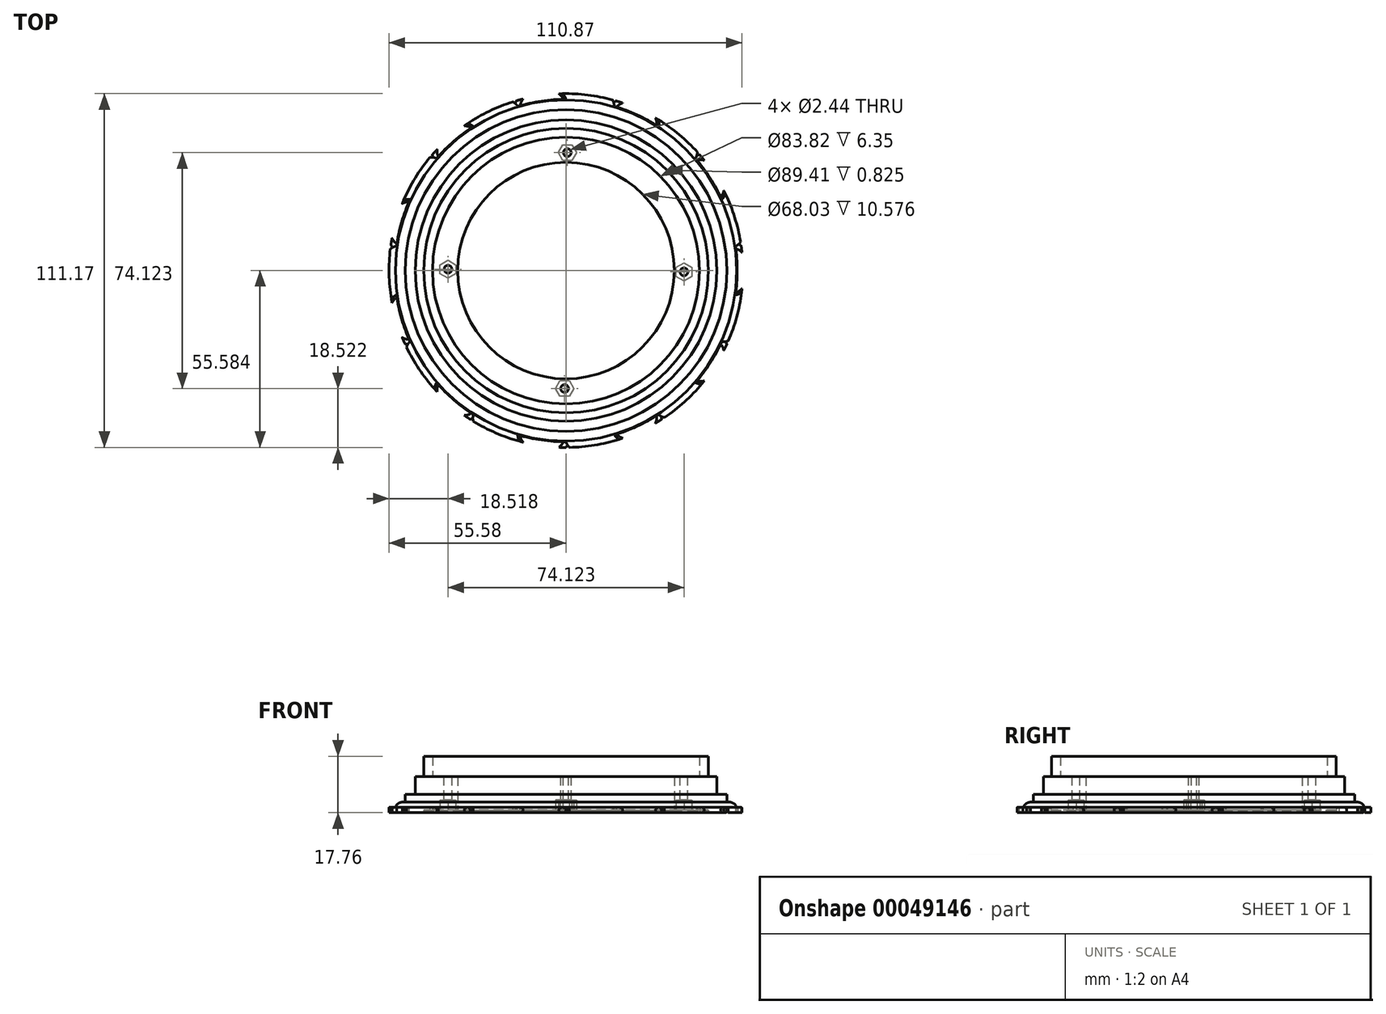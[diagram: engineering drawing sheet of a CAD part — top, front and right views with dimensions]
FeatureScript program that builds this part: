
annotation { "Feature Type Name" : "Feature", "Feature Type Description" : "" }
export const myFeature = defineFeature(function(context is Context, id is Id, definition is map)
    precondition{}
    {
        {
            assignVariable(context, id + "F0", {"name" : "numTeeth", "anyValue" : 11});
        }
        {
            var Q0;
            Q0=qCreatedBy(makeId("Top.planeOp"),FACE);
            var sketch = newSketch(context, id + "F1", { "sketchPlane" : qUnion([Q0])});
            skCircle(sketch, "E0", {"center": v(0, 0) * mm, "radius": 57.15 * mm, "construction": true});
            skLineSegment(sketch, "E1", {"start": v(0, 0) * mm, "end": v(0, 57.15) * mm, "construction": true});
            skCircle(sketch, "E2", {"center": v(0, 3.34) * mm, "radius": 53.8 * mm});
            skCircle(sketch, "E3", {"center": v(0, 3.34) * mm, "radius": 3.34 * mm, "construction": true});
            skLineSegment(sketch, "E4", {"start": v(0, 3.34) * mm, "end": v(-29.09, 48.6) * mm, "construction": true});
            skLineSegment(sketch, "E5", {"start": v(0, 57.15) * mm, "end": v(-29.09, 48.6) * mm, "construction": true});
            skLineSegment(sketch, "E6", {"start": v(-14.54, 52.88) * mm, "end": v(-29.09, 48.6) * mm, "construction": true});
            skLineSegment(sketch, "E7", {"start": v(-14.02, 24.18) * mm, "end": v(-21.82, 50.74) * mm, "construction": true});
            skCircle(sketch, "E8", {"center": v(-14.54, 52.88) * mm, "radius": 7.58 * mm, "construction": true});
            skLineSegment(sketch, "E9", {"start": v(-15.16, 54.97) * mm, "end": v(-16.68, 60.15) * mm, "construction": true});
            skEllipticalArc(sketch, "E10", {});
            skPoint(sketch, "E11", {"position": v(-15.16, 54.97) * mm});
            skLineSegment(sketch, "E12", {"start": v(-15.16, 54.97) * mm, "end": v(0, 54.97) * mm, "construction": true});
            skPoint(sketch, "E13", {"position": v(-7.58, 54.97) * mm});
            skCircle(sketch, "E14", {"center": v(0, 54.97) * mm, "radius": 7.58 * mm, "construction": true});
            skPoint(sketch, "E15", {"position": v(0, 62.55) * mm});
            skEllipticalArc(sketch, "E16", {});
            skCircle(sketch, "E17", {"center": v(0, 3.34) * mm, "radius": 44.7 * mm});
            skEllipticalArc(sketch, "E18.trimOffspring", {});
            skEllipticalArc(sketch, "E19.trimOffspring", {});
            skLineSegment(sketch, "E20", {"start": v(0, 3.34) * mm, "end": v(-8.33, 61.3) * mm, "construction": true});
            skCircle(sketch, "E21", {"center": v(0, 3.34) * mm, "radius": 55.58 * mm});
            skCircle(sketch, "E22", {"center": v(0, 3.34) * mm, "radius": 127 * mm});
            skLineSegment(sketch, "E23", {"start": v(0, 3.34) * mm, "end": v(-127, 3.34) * mm, "construction": true});
            skLineSegment(sketch, "E24", {"start": v(-53.8, 3.34) * mm, "end": v(-55.58, 3.34) * mm, "construction": true});
            skFitSpline(sketch, "E25.0", {"points": [v(-14.94, 56.45) * mm, v(-15.23, 54.97) * mm, v(-14.94, 53.49) * mm, v(-14.22, 52.3) * mm, v(-13.37, 51.41) * mm, v(-12.35, 50.56) * mm, v(-10.78, 49.6) * mm, v(-8.86, 48.81) * mm, v(-7.15, 48.3) * mm, v(-5.35, 47.87) * mm, v(-3.45, 47.59) * mm, v(-1.5, 47.44) * mm, v(0, 47.4) * mm, v(1.5, 47.44) * mm, v(3.45, 47.59) * mm, v(5.35, 47.87) * mm, v(7.15, 48.3) * mm, v(8.86, 48.81) * mm, v(10.78, 49.6) * mm, v(12.35, 50.56) * mm, v(13.37, 51.41) * mm, v(14.22, 52.3) * mm, v(14.94, 53.49) * mm, v(15.23, 54.97) * mm, v(14.94, 56.45) * mm, v(14.22, 57.63) * mm, v(13.37, 58.53) * mm, v(12.35, 59.38) * mm, v(10.78, 60.34) * mm, v(8.86, 61.13) * mm, v(7.15, 61.64) * mm, v(5.35, 62.07) * mm, v(3.45, 62.35) * mm, v(1.5, 62.5) * mm, v(0, 62.54) * mm, v(-1.5, 62.5) * mm, v(-3.45, 62.35) * mm, v(-5.35, 62.07) * mm, v(-7.15, 61.64) * mm, v(-8.86, 61.13) * mm, v(-10.78, 60.34) * mm, v(-12.35, 59.38) * mm, v(-13.37, 58.53) * mm, v(-14.22, 57.63) * mm, v(-14.94, 56.45) * mm, v(-15.23, 54.97) * mm, v(-14.94, 53.49) * mm]});
            skFitSpline(sketch, "E25.1", {"points": [v(0.2, 55.67) * mm, v(0.07, 57.17) * mm, v(-0.63, 58.5) * mm, v(-1.65, 59.44) * mm, v(-2.71, 60.06) * mm, v(-3.94, 60.6) * mm, v(-5.72, 61.07) * mm, v(-7.78, 61.28) * mm, v(-9.57, 61.3) * mm, v(-11.4, 61.2) * mm, v(-13.31, 60.94) * mm, v(-15.23, 60.52) * mm, v(-16.68, 60.14) * mm, v(-18.1, 59.68) * mm, v(-19.94, 59) * mm, v(-21.68, 58.18) * mm, v(-23.28, 57.27) * mm, v(-24.78, 56.3) * mm, v(-26.4, 55) * mm, v(-27.64, 53.63) * mm, v(-28.38, 52.53) * mm, v(-28.94, 51.43) * mm, v(-29.3, 50.1) * mm, v(-29.16, 48.59) * mm, v(-28.46, 47.25) * mm, v(-27.44, 46.32) * mm, v(-26.38, 45.7) * mm, v(-25.15, 45.17) * mm, v(-23.37, 44.7) * mm, v(-21.31, 44.47) * mm, v(-19.52, 44.46) * mm, v(-17.68, 44.56) * mm, v(-15.78, 44.82) * mm, v(-13.86, 45.23) * mm, v(-12.41, 45.62) * mm, v(-11, 46.08) * mm, v(-9.15, 46.77) * mm, v(-7.41, 47.58) * mm, v(-5.8, 48.5) * mm, v(-4.3, 49.47) * mm, v(-2.7, 50.76) * mm, v(-1.45, 52.12) * mm, v(-0.7, 53.23) * mm, v(-0.15, 54.33) * mm, v(0.2, 55.67) * mm, v(0.07, 57.17) * mm, v(-0.63, 58.5) * mm]});
            skLineSegment(sketch, "E26", {"start": v(0, 57.15) * mm, "end": v(0, 62.7) * mm, "construction": true});
            skPoint(sketch, "E27", {"position": v(0, 57.15) * mm});
            skArc(sketch, "E28", {"start": v(0, 57.15) * mm, "mid": v(-15.16, 54.97) * mm, "end": v(-29.09, 48.6) * mm});
            skArc(sketch, "E29", {"start": v(0, 57.15) * mm, "mid": v(-15.16, 54.97) * mm, "end": v(-29.09, 48.6) * mm, "construction": true});
            skCircle(sketch, "E30", {"center": v(0, 3.34) * mm, "radius": 41.91 * mm});
            const initialGuessF1  = {"E10": [-0.014544874279921795, 0.052879249601956, 0.9594931524201487, 0.2817319478845903, 0.015158914102966718, 0.007579457051483363, 0, 0.9887715007809849], "E16": [0, 0.054970482101318274, -1, 0, 0.01515891410296674, 0.0075794570514833666, 1.5707963267948966, 4.71238898038469], "E18.trimOffspring": [0, 0.054970482101318274, -1, 0, 0.01515891410296674, 0.0075794570514833666, 5.294413806398602, 0], "E19.trimOffspring": [-0.014544874279921795, 0.052879249601956, 0.9594931524201485, 0.2817319478845902, 0.015158914102966718, 0.007579457051483363, 1.5707963267948966, 3.141592653589793]};
            skSetInitialGuess(sketch, initialGuessF1);
            skSolve(sketch);
        }
        {
            var Q0;
            Q0=sQuery(id+"F1.wireOp",VERTEX,"E10.start");
            var Q1;
            Q1=sQuery(id+"F1.wireOp",EDGE,"E1");
            cPlane(context, id + "F2", {"entities" : qUnion([Q0, Q1]), "cplaneType" : CPlaneType.LINE_POINT, "offset" : 152.4 * mm, "width" : 152.4 * mm, "height" : 152.4 * mm});
        }
        {
            var Q0;
            Q0=qCreatedBy(id+"F2.planeOp",FACE);
            var sketch = newSketch(context, id + "F3", { "sketchPlane" : qUnion([Q0])});
            skCircle(sketch, "E31", {"center": v(0, 0) * mm, "radius": 0.83 * mm});
            skPoint(sketch, "E31.first.point", {"position": v(-0.82, -0.03) * mm});
            skPoint(sketch, "E31.second.point", {"position": v(0.82, 0.1) * mm});
            skPoint(sketch, "E31.third.point", {"position": v(-0.15, 0.81) * mm});
            skLineSegment(sketch, "E32", {"start": v(-0.82, -0.03) * mm, "end": v(22.8, 0.81) * mm, "construction": true});
            skSolve(sketch);
        }
        {
            var Q0;
            Q0=qSketchRegion(id+"F3",true);
            var Q1;
            Q1=sQuery(id+"F1.wireOp",EDGE,"E10");
            sweep(context, id + "F4", {"profiles" : qUnion([Q0]), "path" : qUnion([Q1])});
        }
        {
            var Q0;
            Q0=sQuery(id+"F1.wireOp",EDGE,"E20");
            cPlane(context, id + "F5", {"entities" : qUnion([Q0]), "cplaneType" : CPlaneType.LINE_ANGLE, "offset" : 152.4 * mm, "angle" : 90 * degree, "width" : 152.4 * mm, "height" : 152.4 * mm});
        }
        {
            var Q0;
            Q0=qCreatedBy(makeId("Right.planeOp"),FACE);
            var sketch = newSketch(context, id + "F6", { "sketchPlane" : qUnion([Q0])});
            skLineSegment(sketch, "E33", {"start": v(3.34, 0) * mm, "end": v(3.34, 43.32) * mm, "construction": true});
            skSolve(sketch);
        }
        {
            var Q0;
            Q0=makeQuery(id+"F4.opSweep","SWEPT_BODY",BODY,{"disambiguationData":[OSD([sQuery(id+"F1.wireOp",EDGE,"E10"),sQuery(id+"F3.wireOp",EDGE,"E31")])]});
            var Q1;
            Q1=qCreatedBy(id+"F5.planeOp",FACE);
            mirror(context, id + "F7", {"operationType" : NewBodyOperationType.ADD, "entities" : qUnion([Q0]), "mirrorPlane" : qUnion([Q1])});
        }
        {
            var Q0;
            {var subQ3=sQuery(id+"F1.wireOp",EDGE,"E2");var subQ5=sQuery(id+"F1.wireOp",EDGE,"E25.1");var subQ7=makeQuery(id+"F1.imprint","INTERSECT",VERTEX,{"derivedFrom":[subQ3,subQ5]});Q0=makeQuery(id+"F1.imprint","IMPRINT",FACE,{"disambiguationData":[TD([[makeQuery(id+"F1.imprint","IMPRINT",EDGE,{"disambiguationData":[TD([[subQ7,-1.0]])],"derivedFrom":subQ3}),-1.0]])]});}
            extrude(context, id + "F8", {"entities" : qUnion([Q0]), "operationType" : NewBodyOperationType.ADD, "endBound" : BoundingType.SYMMETRIC, "depth" : 1.65 * mm});
        }
        {
            var Q0;
            Q0=makeQuery(id+"F4.opSweep","SWEPT_BODY",BODY,{"disambiguationData":[OSD([sQuery(id+"F1.wireOp",EDGE,"E10"),sQuery(id+"F3.wireOp",EDGE,"E31")])]});
            var Q1;
            Q1=sQuery(id+"F6.wireOp",EDGE,"E33");
            circularPattern(context, id + "F9", {"entities" : qUnion([Q0]), "axis" : qUnion([Q1]), "angle" : (360 / getVariable(context, 'numTeeth')) * degree, "instanceCount" : getVariable(context, 'numTeeth')});
        }
        {
            var Q0;
            Q0=makeQuery(id+"F1.imprint","IMPRINT",FACE,{"disambiguationData":[TD([[makeQuery(id+"F1.imprint","IMPRINT",EDGE,{"derivedFrom":sQuery(id+"F1.wireOp",EDGE,"E17")}),-1.0]])]});
            extrude(context, id + "F10", {"entities" : qUnion([Q0]), "operationType" : NewBodyOperationType.ADD, "endBound" : BoundingType.SYMMETRIC, "depth" : 1.65 * mm});
        }
        {
            var Q0;
            Q0=makeQuery(id+"F1.imprint","IMPRINT",FACE,{"disambiguationData":[TD([[makeQuery(id+"F1.imprint","IMPRINT",EDGE,{"derivedFrom":sQuery(id+"F1.wireOp",EDGE,"E22")}),1.0]])]});
            var Q1;
            {var subQ6=sQuery(id+"F1.wireOp",EDGE,"E18.trimOffspring");var subQ8=sQuery(id+"F1.wireOp",EDGE,"E10");var subQ10=makeQuery(id+"F1.imprint","INTERSECT",VERTEX,{"derivedFrom":[subQ8,subQ6]});Q1=makeQuery(id+"F1.imprint","IMPRINT",FACE,{"disambiguationData":[TD([[makeQuery(id+"F1.imprint","IMPRINT",EDGE,{"disambiguationData":[TD([[subQ10,1.0]])],"derivedFrom":subQ8}),1.0]])]});}
            var Q2;
            {var subQ0=sQuery(id+"F1.wireOp",EDGE,"E25.1");var subQ1=sQuery(id+"F1.wireOp",EDGE,"E21");var subQ2=makeQuery(id+"F1.imprint","INTERSECT",VERTEX,{"derivedFrom":[subQ1,subQ0]});Q2=makeQuery(id+"F1.imprint","IMPRINT",FACE,{"disambiguationData":[TD([[makeQuery(id+"F1.imprint","IMPRINT",EDGE,{"disambiguationData":[TD([[subQ2,-1.0]])],"derivedFrom":subQ1}),-1.0]])]});}
            extrude(context, id + "F11", {"entities" : qUnion([Q0, Q1, Q2]), "operationType" : NewBodyOperationType.REMOVE, "endBound" : BoundingType.SYMMETRIC, "oppositeDirection" : true, "depth" : 25.4 * mm});
        }
        {
            var Q0;
            Q0=qCreatedBy(makeId("Right.planeOp"),FACE);
            var sketch = newSketch(context, id + "F12", { "sketchPlane" : qUnion([Q0])});
            skLineSegment(sketch, "E34", {"start": v(-50.36, 0) * mm, "end": v(-50.36, 0.2) * mm});
            skLineSegment(sketch, "E35", {"start": v(-48.07, 2.48) * mm, "end": v(-47.18, 2.48) * mm});
            skLineSegment(sketch, "E36", {"start": v(-47.18, 2.48) * mm, "end": v(-47.18, 4.94) * mm});
            skLineSegment(sketch, "E37", {"start": v(-47.18, 4.94) * mm, "end": v(-44, 4.94) * mm});
            skLineSegment(sketch, "E38", {"start": v(-44, 4.94) * mm, "end": v(-44, 9.3) * mm});
            skLineSegment(sketch, "E39", {"start": v(-44, 10.58) * mm, "end": v(-30.67, 10.58) * mm});
            skLineSegment(sketch, "E40", {"start": v(-30.67, 10.58) * mm, "end": v(-30.67, 0) * mm});
            skLineSegment(sketch, "E41", {"start": v(-30.67, 0) * mm, "end": v(-50.36, 0) * mm});
            skPoint(sketch, "E42.visualSharp", {"position": v(-50.36, 2.48) * mm});
            skArc(sketch, "E42.filletArc", {"start": v(-48.07, 2.48) * mm, "mid": v(-49.69, 1.8) * mm, "end": v(-50.36, 0.2) * mm});
            skLineSegment(sketch, "E43", {"start": v(-44, 9.3) * mm, "end": v(-48.41, 9.3) * mm, "construction": true});
            skLineSegment(sketch, "E44", {"start": v(-48.41, 9.3) * mm, "end": v(-51.55, 9.3) * mm, "construction": true});
            skLineSegment(sketch, "E45", {"start": v(-44, 9.3) * mm, "end": v(-44, 10.58) * mm});
            skSolve(sketch);
        }
        {
            var Q0;
            Q0=makeQuery(id+"F12.imprint","IMPRINT",FACE,{"disambiguationData":[TD([[makeQuery(id+"F12.imprint","IMPRINT",EDGE,{"derivedFrom":sQuery(id+"F12.wireOp",EDGE,"E34")}),-1.0]])]});
            var Q1;
            Q1=sQuery(id+"F6.wireOp",EDGE,"E33");
            revolve(context, id + "F13", {"operationType" : NewBodyOperationType.ADD, "entities" : qUnion([Q0]), "axis" : qUnion([Q1]), "revolveType" : RevolveType.FULL});
        }
        {
            var Q0;
            Q0=makeQuery(id+"F1.imprint","IMPRINT",FACE,{"disambiguationData":[TD([[makeQuery(id+"F1.imprint","IMPRINT",EDGE,{"derivedFrom":sQuery(id+"F1.wireOp",EDGE,"E17")}),1.0]])]});
            extrude(context, id + "F14", {"entities" : qUnion([Q0]), "depth" : 16.93 * mm, "hasSecondDirection" : true, "secondDirectionOppositeDirection" : false, "secondDirectionDepth" : 10.58 * mm});
        }
        {
            var Q0;
            Q0=makeQuery(id+"F13.opRevolve","SWEPT_FACE",FACE,{"disambiguationData":[OSD([sQuery(id+"F12.wireOp",EDGE,"E39")])]});
            var sketch = newSketch(context, id + "F15", { "sketchPlane" : qUnion([Q0])});
            skLineSegment(sketch, "E46", {"start": v(-34.01, 3.76) * mm, "end": v(-37.06, 3.76) * mm});
            skCircle(sketch, "E47.cCircle", {"center": v(-37.06, 3.76) * mm, "radius": 2.48 * mm, "construction": true});
            skLineSegment(sketch, "E47.0", {"start": v(-37.06, 6.62) * mm, "end": v(-34.59, 5.2) * mm});
            skLineSegment(sketch, "E47.1", {"start": v(-34.59, 5.2) * mm, "end": v(-34.59, 2.33) * mm});
            skLineSegment(sketch, "E47.2", {"start": v(-34.59, 2.33) * mm, "end": v(-37.06, 0.9) * mm});
            skLineSegment(sketch, "E47.3", {"start": v(-37.06, 0.9) * mm, "end": v(-39.54, 2.33) * mm});
            skLineSegment(sketch, "E47.4", {"start": v(-39.54, 2.33) * mm, "end": v(-39.54, 5.2) * mm});
            skLineSegment(sketch, "E47.5", {"start": v(-39.54, 5.2) * mm, "end": v(-37.06, 6.62) * mm});
            skPoint(sketch, "E47.0.midPoint", {"position": v(-35.82, 5.9) * mm});
            skLineSegment(sketch, "E48.1.0", {"start": v(1.01, -36.2) * mm, "end": v(-1.85, -36.2) * mm});
            skLineSegment(sketch, "E48.1.1", {"start": v(2.44, -33.72) * mm, "end": v(1.01, -36.2) * mm});
            skLineSegment(sketch, "E48.1.2", {"start": v(1.01, -31.24) * mm, "end": v(2.44, -33.72) * mm});
            skLineSegment(sketch, "E48.1.3", {"start": v(-1.85, -36.2) * mm, "end": v(-3.28, -33.72) * mm});
            skLineSegment(sketch, "E48.1.4", {"start": v(-3.28, -33.72) * mm, "end": v(-1.85, -31.24) * mm});
            skLineSegment(sketch, "E48.1.5", {"start": v(-1.85, -31.24) * mm, "end": v(1.01, -31.24) * mm});
            skLineSegment(sketch, "E48.2.0", {"start": v(39.54, 4.36) * mm, "end": v(39.54, 1.5) * mm});
            skLineSegment(sketch, "E48.2.1", {"start": v(37.06, 5.79) * mm, "end": v(39.54, 4.36) * mm});
            skLineSegment(sketch, "E48.2.2", {"start": v(34.59, 4.36) * mm, "end": v(37.06, 5.79) * mm});
            skLineSegment(sketch, "E48.2.3", {"start": v(39.54, 1.5) * mm, "end": v(37.06, 0.07) * mm});
            skLineSegment(sketch, "E48.2.4", {"start": v(37.06, 0.07) * mm, "end": v(34.59, 1.5) * mm});
            skLineSegment(sketch, "E48.2.5", {"start": v(34.59, 1.5) * mm, "end": v(34.59, 4.36) * mm});
            skLineSegment(sketch, "E48.3.0", {"start": v(-1.01, 42.88) * mm, "end": v(1.85, 42.88) * mm});
            skLineSegment(sketch, "E48.3.1", {"start": v(-2.44, 40.4) * mm, "end": v(-1.01, 42.88) * mm});
            skLineSegment(sketch, "E48.3.2", {"start": v(-1.01, 37.93) * mm, "end": v(-2.44, 40.4) * mm});
            skLineSegment(sketch, "E48.3.3", {"start": v(1.85, 42.88) * mm, "end": v(3.28, 40.4) * mm});
            skLineSegment(sketch, "E48.3.4", {"start": v(3.28, 40.4) * mm, "end": v(1.85, 37.93) * mm});
            skLineSegment(sketch, "E48.3.5", {"start": v(1.85, 37.93) * mm, "end": v(-1.01, 37.93) * mm});
            skPoint(sketch, "E48.center", {"position": v(0, 3.34) * mm});
            skCircle(sketch, "E49", {"center": v(-37.06, 3.76) * mm, "radius": 1.22 * mm});
            skCircle(sketch, "E50.1.0", {"center": v(-0.42, -33.72) * mm, "radius": 1.22 * mm});
            skCircle(sketch, "E50.2.0", {"center": v(37.06, 2.93) * mm, "radius": 1.22 * mm});
            skCircle(sketch, "E50.3.0", {"center": v(0.42, 40.4) * mm, "radius": 1.22 * mm});
            skPoint(sketch, "E51.0.midPoint", {"position": v(-49.78, 6.28) * mm});
            skSolve(sketch);
        }
        {
            var Q0;
            Q0=makeQuery(id+"F15.imprint","IMPRINT",FACE,{"disambiguationData":[TD([[makeQuery(id+"F15.imprint","IMPRINT",EDGE,{"derivedFrom":sQuery(id+"F15.wireOp",EDGE,"E49")}),1.0]])]});
            var Q1;
            Q1=makeQuery(id+"F15.imprint","IMPRINT",FACE,{"disambiguationData":[TD([[makeQuery(id+"F15.imprint","IMPRINT",EDGE,{"derivedFrom":sQuery(id+"F15.wireOp",EDGE,"E50.3.0")}),1.0]])]});
            var Q2;
            Q2=makeQuery(id+"F15.imprint","IMPRINT",FACE,{"disambiguationData":[TD([[makeQuery(id+"F15.imprint","IMPRINT",EDGE,{"derivedFrom":sQuery(id+"F15.wireOp",EDGE,"E50.2.0")}),1.0]])]});
            var Q3;
            Q3=makeQuery(id+"F15.imprint","IMPRINT",FACE,{"disambiguationData":[TD([[makeQuery(id+"F15.imprint","IMPRINT",EDGE,{"derivedFrom":sQuery(id+"F15.wireOp",EDGE,"E50.1.0")}),1.0]])]});
            extrude(context, id + "F16", {"entities" : qUnion([Q0, Q1, Q2, Q3]), "operationType" : NewBodyOperationType.REMOVE, "endBound" : BoundingType.THROUGH_ALL, "oppositeDirection" : true, "depth" : 25.4 * mm});
        }
        {
            var Q0;
            Q0=makeQuery(id+"F1.imprint","IMPRINT",FACE,{"disambiguationData":[TD([[makeQuery(id+"F1.imprint","IMPRINT",EDGE,{"derivedFrom":sQuery(id+"F1.wireOp",EDGE,"E30")}),1.0]])]});
            var sketch = newSketch(context, id + "F17", { "sketchPlane" : qUnion([Q0])});
            skLineSegment(sketch, "E52.0", {"start": v(-1.01, 37.93) * mm, "end": v(-2.44, 40.4) * mm});
            skLineSegment(sketch, "E52.1", {"start": v(-2.44, 40.4) * mm, "end": v(-1.01, 42.88) * mm});
            skLineSegment(sketch, "E52.2", {"start": v(-1.01, 42.88) * mm, "end": v(1.85, 42.88) * mm});
            skLineSegment(sketch, "E52.3", {"start": v(1.85, 42.88) * mm, "end": v(3.28, 40.4) * mm});
            skLineSegment(sketch, "E52.4", {"start": v(3.28, 40.4) * mm, "end": v(1.85, 37.93) * mm});
            skLineSegment(sketch, "E52.5", {"start": v(1.85, 37.93) * mm, "end": v(-1.01, 37.93) * mm});
            skLineSegment(sketch, "E53.7", {"start": v(-1.85, -36.2) * mm, "end": v(-3.28, -33.72) * mm});
            skLineSegment(sketch, "E53.8", {"start": v(-3.28, -33.72) * mm, "end": v(-1.85, -31.24) * mm});
            skLineSegment(sketch, "E53.9", {"start": v(-1.85, -31.24) * mm, "end": v(1.01, -31.24) * mm});
            skLineSegment(sketch, "E53.10", {"start": v(1.01, -31.24) * mm, "end": v(2.44, -33.72) * mm});
            skLineSegment(sketch, "E53.11", {"start": v(2.44, -33.72) * mm, "end": v(1.01, -36.2) * mm});
            skLineSegment(sketch, "E53.12", {"start": v(1.01, -36.2) * mm, "end": v(-1.85, -36.2) * mm});
            skLineSegment(sketch, "E54.13", {"start": v(-39.54, 5.2) * mm, "end": v(-37.06, 6.62) * mm});
            skLineSegment(sketch, "E54.14", {"start": v(-37.06, 6.62) * mm, "end": v(-34.59, 5.2) * mm});
            skLineSegment(sketch, "E54.15", {"start": v(-34.59, 5.2) * mm, "end": v(-34.59, 2.33) * mm});
            skLineSegment(sketch, "E54.16", {"start": v(-34.59, 2.33) * mm, "end": v(-37.06, 0.9) * mm});
            skLineSegment(sketch, "E54.17", {"start": v(-37.06, 0.9) * mm, "end": v(-39.54, 2.33) * mm});
            skLineSegment(sketch, "E54.18", {"start": v(-39.54, 2.33) * mm, "end": v(-39.54, 5.2) * mm});
            skLineSegment(sketch, "E55.19", {"start": v(34.59, 1.5) * mm, "end": v(34.59, 4.36) * mm});
            skLineSegment(sketch, "E55.20", {"start": v(34.59, 4.36) * mm, "end": v(37.06, 5.79) * mm});
            skLineSegment(sketch, "E55.21", {"start": v(37.06, 5.79) * mm, "end": v(39.54, 4.36) * mm});
            skLineSegment(sketch, "E55.22", {"start": v(39.54, 4.36) * mm, "end": v(39.54, 1.5) * mm});
            skLineSegment(sketch, "E55.23", {"start": v(39.54, 1.5) * mm, "end": v(37.06, 0.07) * mm});
            skLineSegment(sketch, "E55.24", {"start": v(37.06, 0.07) * mm, "end": v(34.59, 1.5) * mm});
            skSolve(sketch);
        }
        {
            var Q0;
            Q0=qSketchRegion(id+"F17",true);
            extrude(context, id + "F18", {"entities" : qUnion([Q0]), "operationType" : NewBodyOperationType.REMOVE, "depth" : 3.17 * mm});
        }
    });
